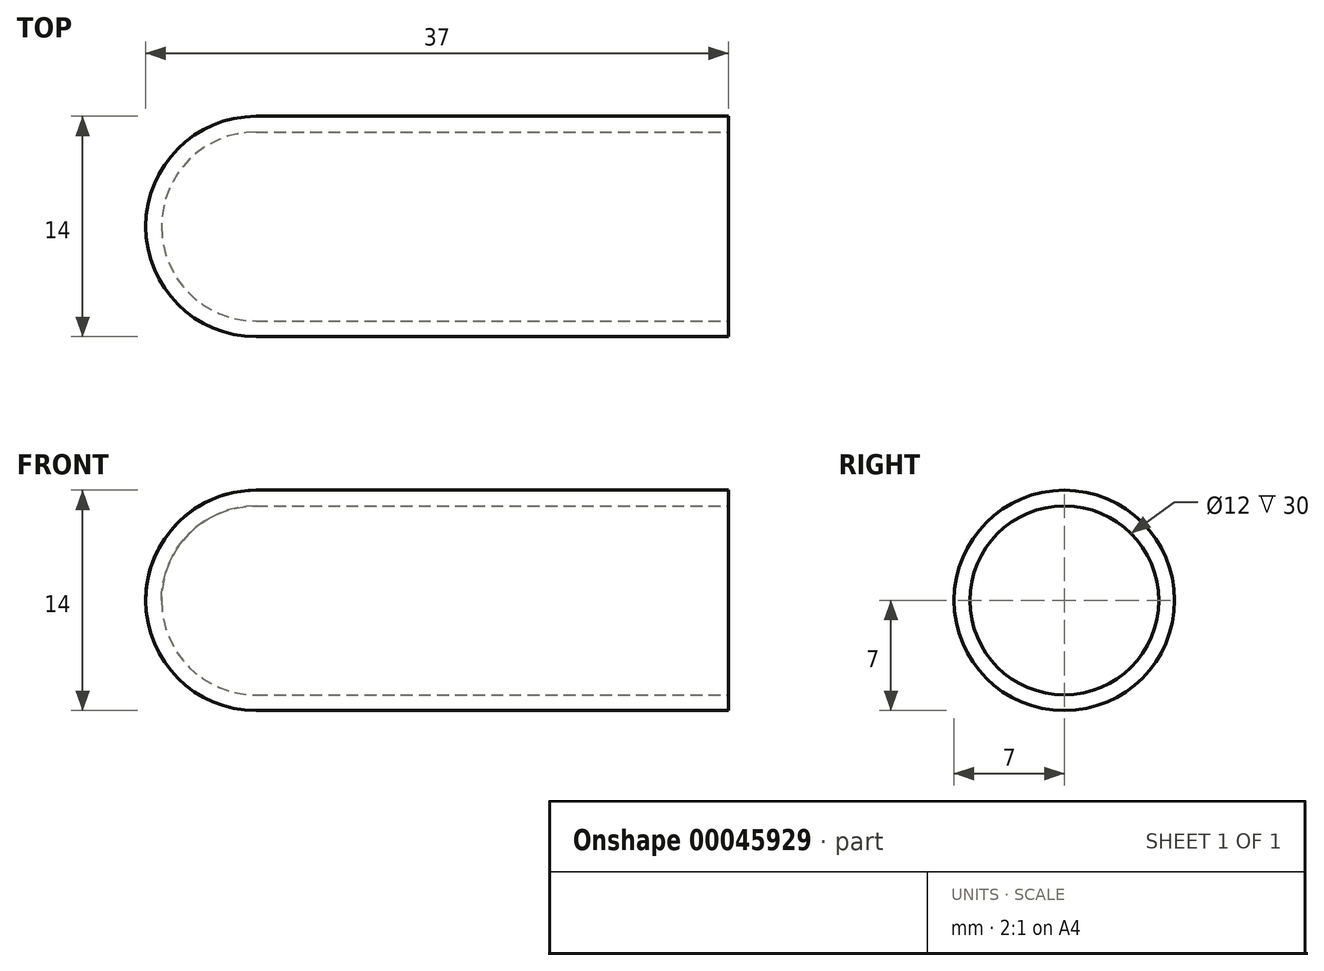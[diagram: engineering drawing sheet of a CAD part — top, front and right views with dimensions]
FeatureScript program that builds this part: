
annotation { "Feature Type Name" : "Feature", "Feature Type Description" : "" }
export const myFeature = defineFeature(function(context is Context, id is Id, definition is map)
    precondition{}
    {
        {
            var Q0;
            Q0=qCreatedBy(makeId("Front.planeOp"),FACE);
            var sketch = newSketch(context, id + "F0", { "sketchPlane" : qUnion([Q0])});
            skLineSegment(sketch, "E0", {"start": v(0, 7) * mm, "end": v(-30, 7) * mm});
            skArc(sketch, "E1", {"start": v(-30, 7) * mm, "mid": v(-34.95, 4.95) * mm, "end": v(-37, 0) * mm});
            skLineSegment(sketch, "E2.MirrorCS", {"start": v(0, -7) * mm, "end": v(-30, -7) * mm});
            skArc(sketch, "E3.MirrorCS", {"start": v(-30, -7) * mm, "mid": v(-34.95, -4.95) * mm, "end": v(-37, 0) * mm});
            skLineSegment(sketch, "E4.0", {"start": v(0, 6) * mm, "end": v(-30, 6) * mm});
            skArc(sketch, "E4.1", {"start": v(-30, 6) * mm, "mid": v(-34.24, 4.24) * mm, "end": v(-36, 0) * mm});
            skArc(sketch, "E4.2", {"start": v(-30, -6) * mm, "mid": v(-34.24, -4.24) * mm, "end": v(-36, 0) * mm});
            skLineSegment(sketch, "E4.3", {"start": v(0, -6) * mm, "end": v(-30, -6) * mm});
            skLineSegment(sketch, "E5", {"start": v(0, 7) * mm, "end": v(0, 6) * mm});
            skLineSegment(sketch, "E6.trimOffspring", {"start": v(0, -6) * mm, "end": v(0, -7) * mm});
            skLineSegment(sketch, "E7", {"start": v(0, 0) * mm, "end": v(-36, 0) * mm});
            skLineSegment(sketch, "E8", {"start": v(-37, 0) * mm, "end": v(-36, 0) * mm});
            skSolve(sketch);
        }
        {
            var Q0;
            Q0=makeQuery(id+"F0.imprint","IMPRINT",FACE,{"disambiguationData":[TD([[makeQuery(id+"F0.imprint","IMPRINT",EDGE,{"derivedFrom":sQuery(id+"F0.wireOp",EDGE,"E0")}),1.0]])]});
            var Q1;
            Q1=sQuery(id+"F0.wireOp",EDGE,"E7");
            revolve(context, id + "F1", {"entities" : qUnion([Q0]), "axis" : qUnion([Q1]), "revolveType" : RevolveType.FULL});
        }
    });
